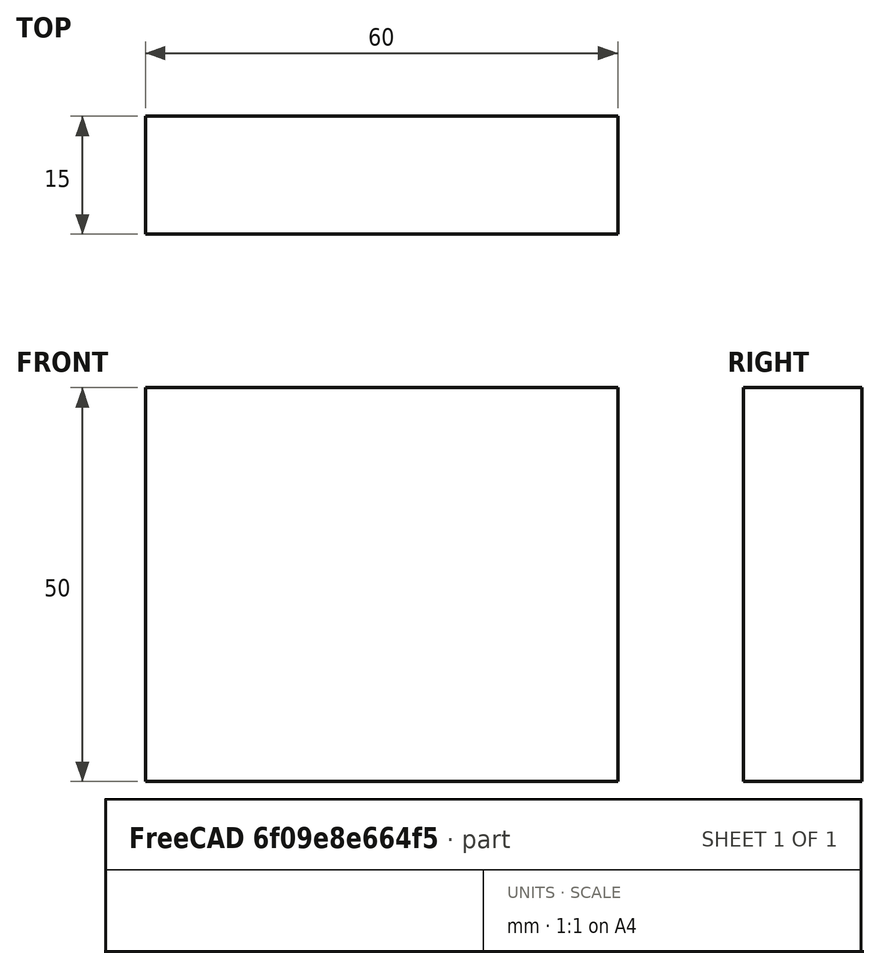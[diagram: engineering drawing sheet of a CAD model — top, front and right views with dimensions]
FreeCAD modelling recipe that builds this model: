
FCSTD DOCUMENT  (FreeCAD 0.15R4671 (Git))
Label: Flat Bar 60x15 EN10058 S235JR
License: All rights reserved
LicenseURL: http://en.wikipedia.org/wiki/All_rights_reserved
objects: Sketcher::SketchObject×1, Part::Extrusion×1
note: 2 computed .brp shape members not serialized (recipe doc carries the construction recipe); baked Part::Feature solids carry a one-line shape summary decoded from their .brp

FEATURE [Sketcher::SketchObject] Sketch
  sketch-geometry (4):
    g0: LineSegment StartX=-30 StartY=-7.5 StartZ=0 EndX=30 EndY=-7.5 EndZ=0
    g1: LineSegment StartX=30 StartY=-7.5 StartZ=0 EndX=30 EndY=7.5 EndZ=0
    g2: LineSegment StartX=30 StartY=7.5 StartZ=0 EndX=-30 EndY=7.5 EndZ=0
    g3: LineSegment StartX=-30 StartY=7.5 StartZ=0 EndX=-30 EndY=-7.5 EndZ=0
  constraints (12):
    c: Coincident(g0,g1)
    c: Coincident(g1,g2)
    c: Coincident(g2,g3)
    c: Coincident(g3,g0)
    c: Horizontal(g0)
    c: Horizontal(g2)
    c: Vertical(g1)
    c: Vertical(g3)
    c: Symmetric(g1,g2,g-2)
    c: Symmetric(g0,g1,g-1)
    c: DistanceY(g1) = 15
    c: DistanceX(g0) = 60
FEATURE [Part::Extrusion] Extrude  label="Flat Bar 60x15 EN10058 S235JR"
  Base = -> Sketch
  Dir = (0,0,50)
  Solid = true
